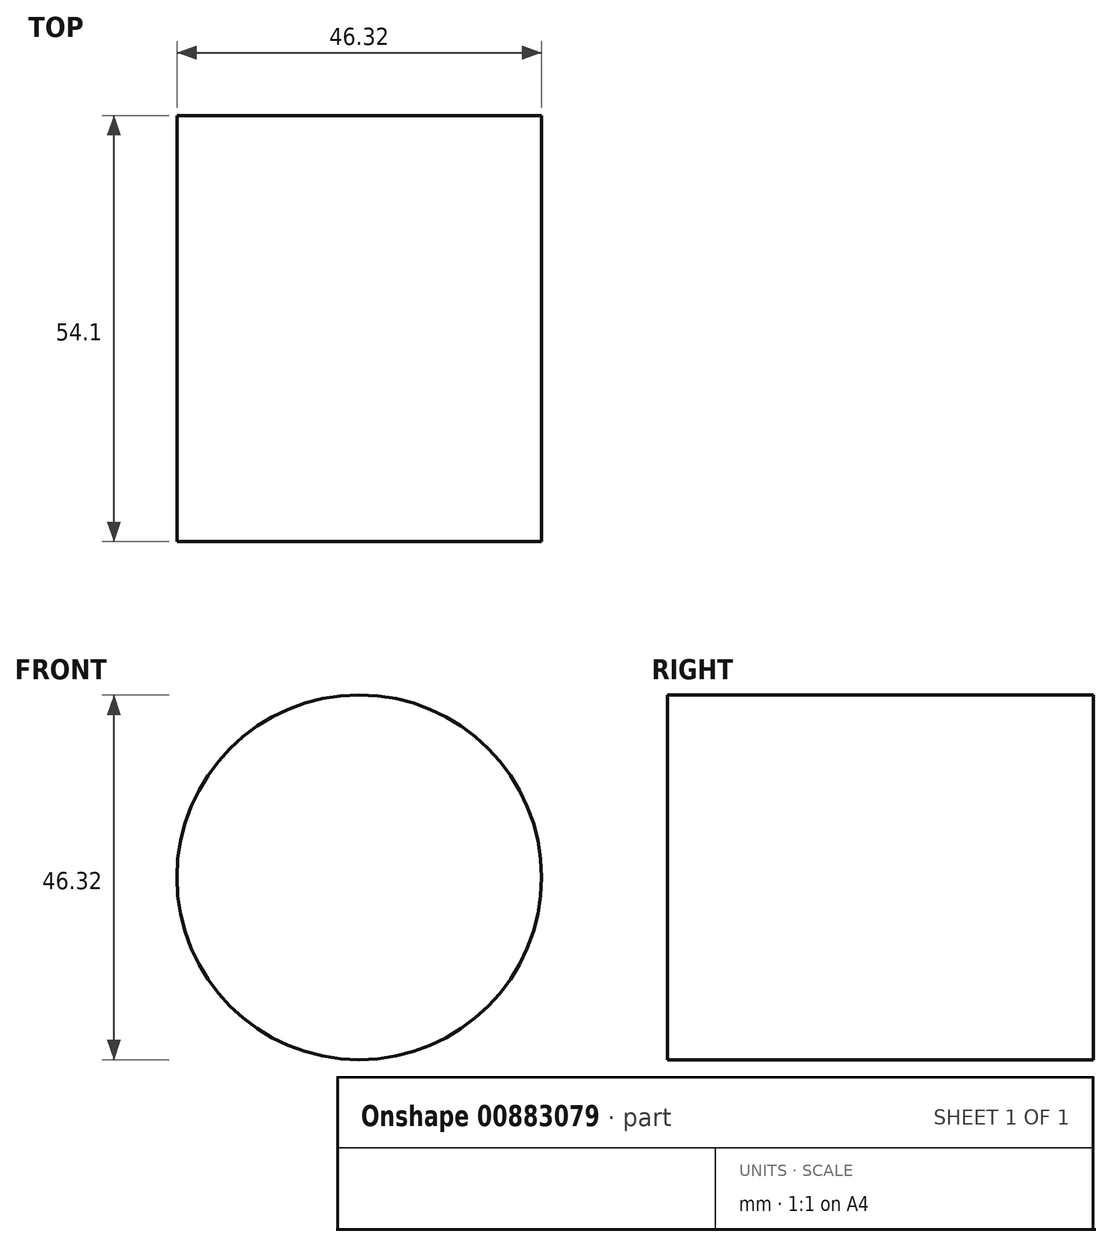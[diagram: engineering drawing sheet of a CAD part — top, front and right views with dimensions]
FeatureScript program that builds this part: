
annotation { "Feature Type Name" : "Feature", "Feature Type Description" : "" }
export const myFeature = defineFeature(function(context is Context, id is Id, definition is map)
    precondition{}
    {
        {
            var Q0;
            Q0=qCreatedBy(makeId("Front.planeOp"),FACE);
            var sketch = newSketch(context, id + "F0", { "sketchPlane" : qUnion([Q0])});
            skCircle(sketch, "E0", {"center": v(0, 0) * mm, "radius": 23.16 * mm});
            skSolve(sketch);
        }
        {
            var Q0;
            Q0=makeQuery(id+"F0.imprint","IMPRINT",FACE,{"disambiguationData":[TD([[makeQuery(id+"F0.imprint","IMPRINT",EDGE,{"derivedFrom":sQuery(id+"F0.wireOp",EDGE,"E0")}),1.0]])]});
            extrude(context, id + "F1", {"entities" : qUnion([Q0]), "depth" : 54.1 * mm, "offsetDistance" : 25.4 * mm});
        }
    });
